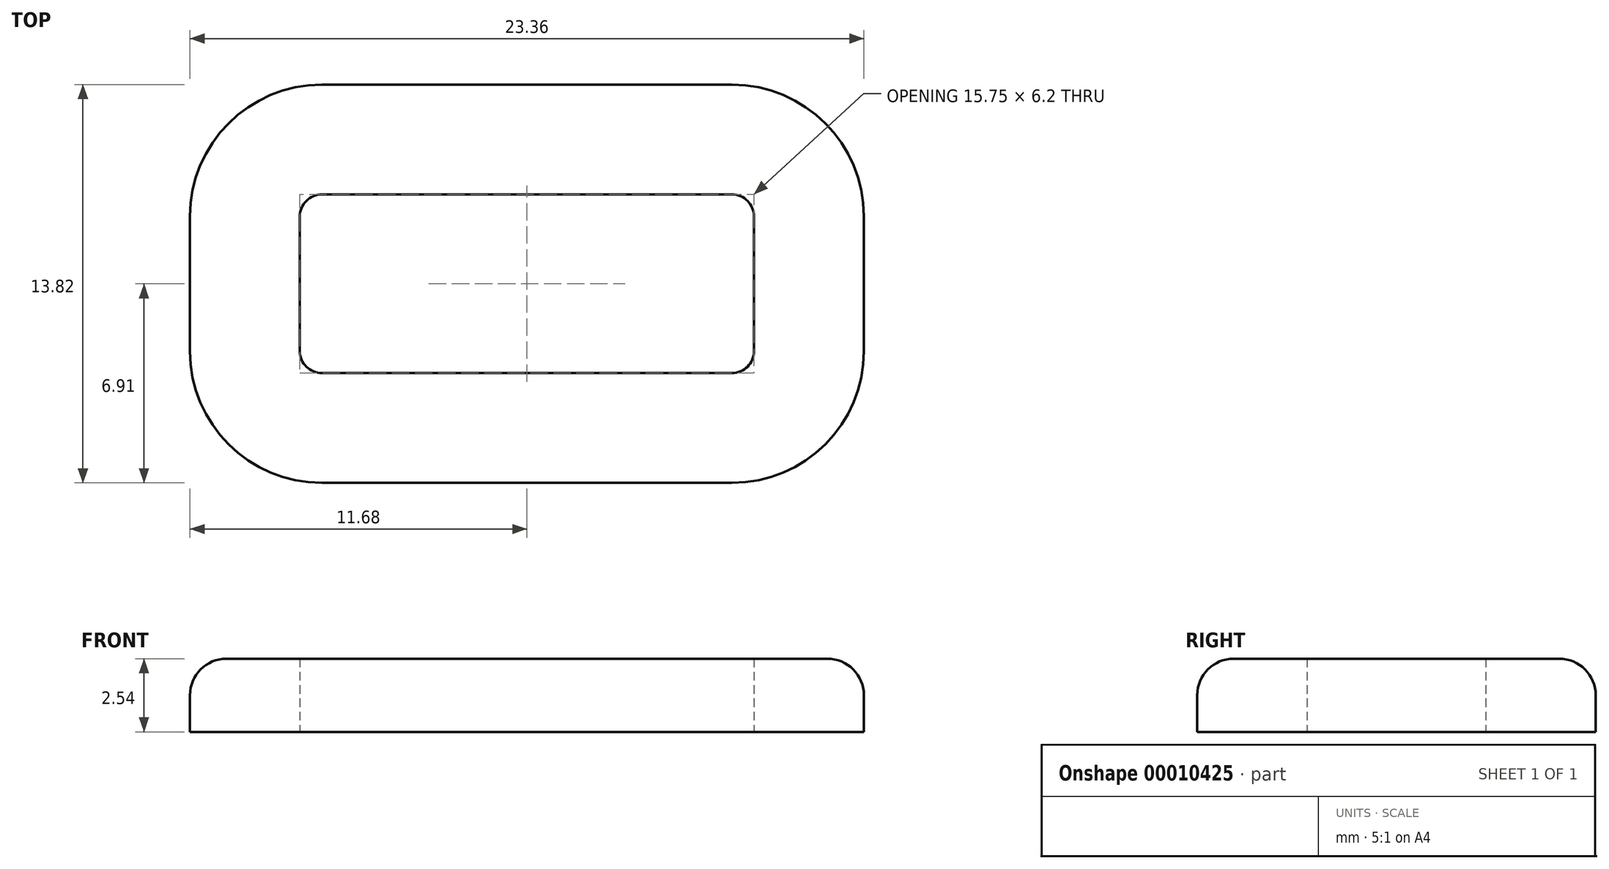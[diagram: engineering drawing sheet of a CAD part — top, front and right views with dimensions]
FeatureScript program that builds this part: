
annotation { "Feature Type Name" : "Feature", "Feature Type Description" : "" }
export const myFeature = defineFeature(function(context is Context, id is Id, definition is map)
    precondition{}
    {
        {
            var Q0;
            Q0=qCreatedBy(makeId("Top.planeOp"),FACE);
            var sketch = newSketch(context, id + "F0", { "sketchPlane" : qUnion([Q0])});
            skLineSegment(sketch, "E0.rect.bottom", {"start": v(7.11, 3.1) * mm, "end": v(-7.11, 3.1) * mm});
            skLineSegment(sketch, "E0.rect.top", {"start": v(7.11, -3.1) * mm, "end": v(-7.11, -3.1) * mm});
            skLineSegment(sketch, "E0.rect.left", {"start": v(7.87, 2.34) * mm, "end": v(7.87, -2.34) * mm});
            skLineSegment(sketch, "E0.rect.right", {"start": v(-7.87, 2.34) * mm, "end": v(-7.87, -2.34) * mm});
            skPoint(sketch, "E0.rect.middle", {"position": v(0, 0) * mm});
            skPoint(sketch, "E1.visualSharp", {"position": v(-7.87, 3.1) * mm});
            skArc(sketch, "E1.filletArc", {"start": v(-7.11, 3.1) * mm, "mid": v(-7.65, 2.88) * mm, "end": v(-7.87, 2.34) * mm});
            skPoint(sketch, "E2.visualSharp", {"position": v(-7.87, -3.1) * mm});
            skArc(sketch, "E2.filletArc", {"start": v(-7.87, -2.34) * mm, "mid": v(-7.65, -2.88) * mm, "end": v(-7.11, -3.1) * mm});
            skPoint(sketch, "E3.visualSharp", {"position": v(7.87, -3.1) * mm});
            skArc(sketch, "E3.filletArc", {"start": v(7.11, -3.1) * mm, "mid": v(7.65, -2.88) * mm, "end": v(7.87, -2.34) * mm});
            skPoint(sketch, "E4.visualSharp", {"position": v(7.87, 3.1) * mm});
            skArc(sketch, "E4.filletArc", {"start": v(7.87, 2.34) * mm, "mid": v(7.65, 2.88) * mm, "end": v(7.11, 3.1) * mm});
            skArc(sketch, "E5.0", {"start": v(-7.11, 6.9) * mm, "mid": v(-10.34, 5.57) * mm, "end": v(-11.68, 2.34) * mm});
            skLineSegment(sketch, "E5.1", {"start": v(7.11, 6.9) * mm, "end": v(-7.11, 6.9) * mm});
            skArc(sketch, "E5.2", {"start": v(11.68, 2.34) * mm, "mid": v(10.34, 5.57) * mm, "end": v(7.11, 6.9) * mm});
            skLineSegment(sketch, "E5.3", {"start": v(11.68, 2.34) * mm, "end": v(11.68, -2.34) * mm});
            skArc(sketch, "E5.4", {"start": v(7.11, -6.9) * mm, "mid": v(10.34, -5.57) * mm, "end": v(11.68, -2.34) * mm});
            skLineSegment(sketch, "E5.5", {"start": v(-11.68, 2.34) * mm, "end": v(-11.68, -2.34) * mm});
            skLineSegment(sketch, "E5.6", {"start": v(7.11, -6.9) * mm, "end": v(-7.11, -6.9) * mm});
            skArc(sketch, "E5.7", {"start": v(-11.68, -2.34) * mm, "mid": v(-10.34, -5.57) * mm, "end": v(-7.11, -6.9) * mm});
            skSolve(sketch);
        }
        {
            var Q0;
            Q0=makeQuery(id+"F0.imprint","IMPRINT",FACE,{"disambiguationData":[TD([[makeQuery(id+"F0.imprint","IMPRINT",EDGE,{"derivedFrom":sQuery(id+"F0.wireOp",EDGE,"E0.rect.bottom")}),-1.0]])]});
            extrude(context, id + "F1", {"entities" : qUnion([Q0]), "depth" : 2.54 * mm});
        }
        {
            var Q0;
            Q0=makeQuery(id+"F1.opExtrude","CAP_EDGE",EDGE,{"disambiguationData":[OSD([sQuery(id+"F0.wireOp",EDGE,"E5.1")])],"isStart":false});
            var Q1;
            Q1=makeQuery(id+"F1.opExtrude","CAP_EDGE",EDGE,{"disambiguationData":[OSD([sQuery(id+"F0.wireOp",EDGE,"E5.2")])],"isStart":false});
            var Q2;
            Q2=makeQuery(id+"F1.opExtrude","CAP_EDGE",EDGE,{"disambiguationData":[OSD([sQuery(id+"F0.wireOp",EDGE,"E5.3")])],"isStart":false});
            var Q3;
            Q3=makeQuery(id+"F1.opExtrude","CAP_EDGE",EDGE,{"disambiguationData":[OSD([sQuery(id+"F0.wireOp",EDGE,"E5.4")])],"isStart":false});
            var Q4;
            Q4=makeQuery(id+"F1.opExtrude","CAP_EDGE",EDGE,{"disambiguationData":[OSD([sQuery(id+"F0.wireOp",EDGE,"E5.6")])],"isStart":false});
            var Q5;
            Q5=makeQuery(id+"F1.opExtrude","CAP_EDGE",EDGE,{"disambiguationData":[OSD([sQuery(id+"F0.wireOp",EDGE,"E5.7")])],"isStart":false});
            var Q6;
            Q6=makeQuery(id+"F1.opExtrude","CAP_EDGE",EDGE,{"disambiguationData":[OSD([sQuery(id+"F0.wireOp",EDGE,"E5.5")])],"isStart":false});
            var Q7;
            Q7=makeQuery(id+"F1.opExtrude","CAP_EDGE",EDGE,{"disambiguationData":[OSD([sQuery(id+"F0.wireOp",EDGE,"E5.0")])],"isStart":false});
            fillet(context, id + "F2", {"entities" : qUnion([Q0, Q1, Q2, Q3, Q4, Q5, Q6, Q7]), "radius" : 1.27 * mm, "tangentPropagation" : true, "allowEdgeOverflow" : false});
        }
    });
